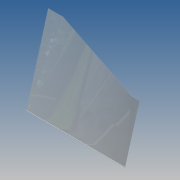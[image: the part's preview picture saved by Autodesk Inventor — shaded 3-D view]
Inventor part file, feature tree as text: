
AUTODESK INVENTOR PART (.ipt)
format: ipt  version: 2013 SP2 (Build 170200200, 200)  size: 153,088 bytes
history: native  units: in
note: dims shown in document units (in); Inventor stores cm internally (conversion verified against a paired STEP export)
features: extrude x5, sketch x5, other x4, loft x1
ambient origin geometry x8: Origin, YZ Plane, XZ Plane, XY Plane, X Axis, Y Axis, Z Axis, Center Point
bodies: Solid1 (feature_tree)
feature tree (15):
  extrude  "base"  Depth=1.0in
  other  "right"
  extrude  "upRight"  Depth=0.0481in
  extrude  "outRight"  Depth=10.0in
  other  "left"
  extrude  "upLeft"  TaperAngle=30.0deg  [1 undecoded]
  extrude  "outLeft"  Depth=0.25in
  loft  "Loft3"
  sketch  "Sketch1"  dims[d0=136.0in d1=1.0in]
  sketch  "Sketch7"  dims[d2=0.25in d3=0.0in d4=0.0481in]
  sketch  "Sketch8"  dims[d34=80.0in d35=0.0in d36=10.0in]
  sketch  "Sketch9"  dims[d37=0.25in d38=0.0in d39=30.0deg]
  sketch  "Sketch10"  dims[d40=0.5in d41=0.25in d42=100.0in d43=0.0in d44=20.0in d45=0.25in d46=0.0in d47=0.0in d48=90.0deg d49=0.0in d50=90.0deg]
  other  "Edges5"
  other  "Edges6"
note: 1 required parameter value undecoded (feature->parameter linkage not recoverable at this tier; creation-order binding heuristic only, values carry confidence <= 0.55)
